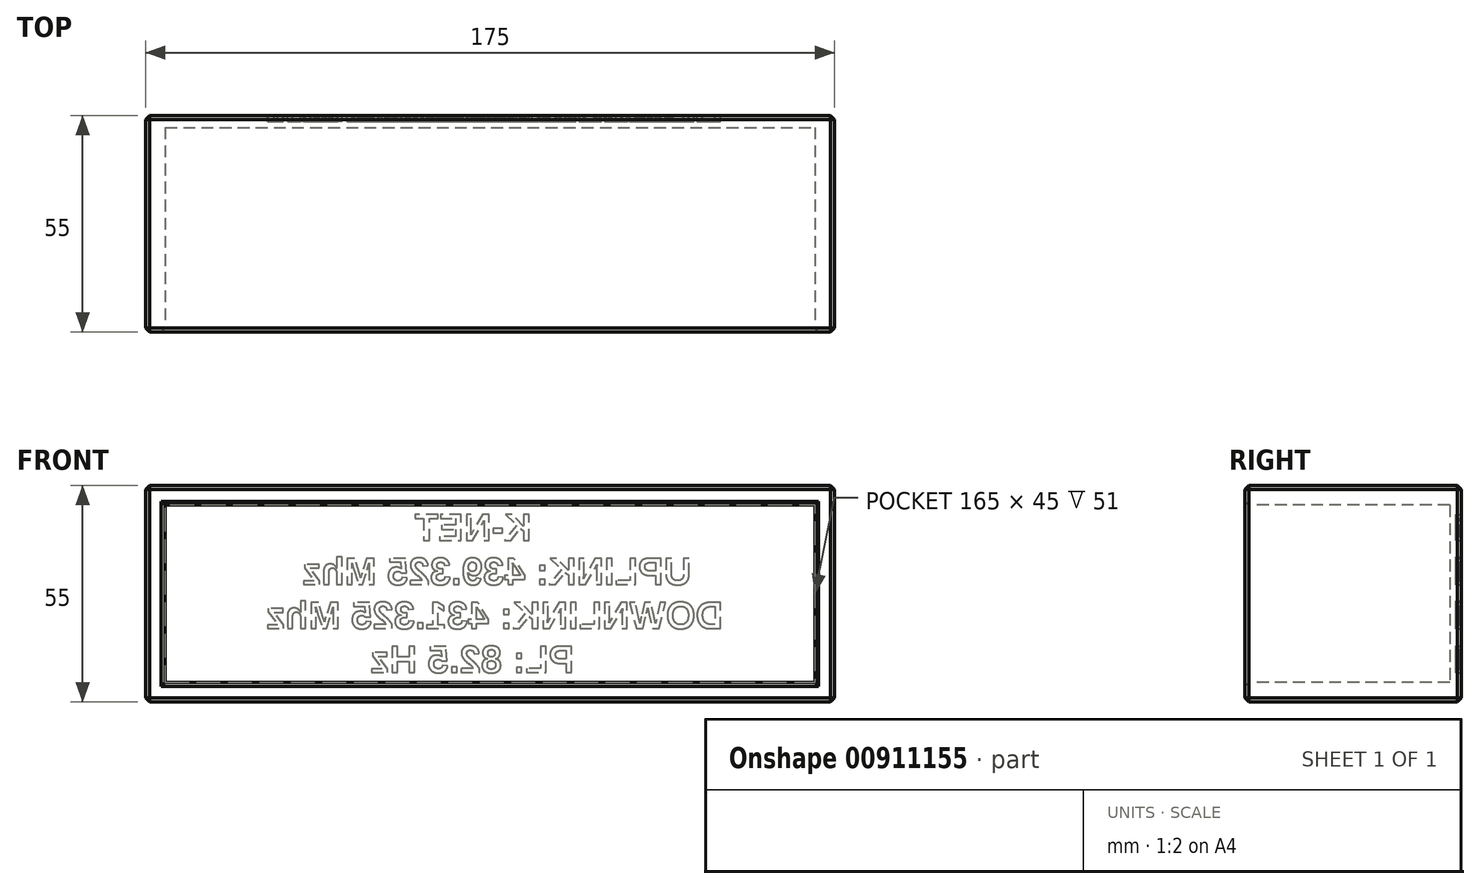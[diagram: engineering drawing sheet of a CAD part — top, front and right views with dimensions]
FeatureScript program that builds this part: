
annotation { "Feature Type Name" : "Feature", "Feature Type Description" : "" }
export const myFeature = defineFeature(function(context is Context, id is Id, definition is map)
    precondition{}
    {
        {
            var Q0;
            Q0=qCreatedBy(makeId("Front.planeOp"),FACE);
            var sketch = newSketch(context, id + "F0", { "sketchPlane" : qUnion([Q0])});
            skLineSegment(sketch, "E0.bottom", {"start": v(-83, 23) * mm, "end": v(92, 23) * mm});
            skLineSegment(sketch, "E0.top", {"start": v(-83, -32) * mm, "end": v(92, -32) * mm});
            skLineSegment(sketch, "E0.left", {"start": v(-83, 23) * mm, "end": v(-83, -32) * mm});
            skLineSegment(sketch, "E0.right", {"start": v(92, 23) * mm, "end": v(92, -32) * mm});
            skSolve(sketch);
        }
        {
            var Q0;
            Q0 = qSketchRegion(id + "F0", true);
            extrude(context, id + "F1", {"entities" : qUnion([Q0]), "depth" : 55 * mm, "offsetDistance" : 25 * mm});
        }
        {
            var Q0;
            Q0=makeQuery(id+"F1.opExtrude","CAP_FACE",FACE,{"disambiguationData":[OSD([sQuery(id+"F0.wireOp",EDGE,"E0.bottom"),sQuery(id+"F0.wireOp",EDGE,"E0.top"),sQuery(id+"F0.wireOp",EDGE,"E0.left"),sQuery(id+"F0.wireOp",EDGE,"E0.right")])],"isStart":false});
            var sketch = newSketch(context, id + "F2", { "sketchPlane" : qUnion([Q0])});
            skLineSegment(sketch, "E1.bottom", {"start": v(-78, 18) * mm, "end": v(87, 18) * mm});
            skLineSegment(sketch, "E1.top", {"start": v(-78, -27) * mm, "end": v(87, -27) * mm});
            skLineSegment(sketch, "E1.left", {"start": v(-78, 18) * mm, "end": v(-78, -27) * mm});
            skLineSegment(sketch, "E1.right", {"start": v(87, 18) * mm, "end": v(87, -27) * mm});
            skSolve(sketch);
        }
        {
            var Q0;
            Q0 = qSketchRegion(id + "F2", true);
            extrude(context, id + "F3", {"entities" : qUnion([Q0]), "operationType" : NewBodyOperationType.REMOVE, "oppositeDirection" : true, "depth" : 52 * mm, "offsetDistance" : 25 * mm});
        }
        {
            var Q0;
            Q0=makeQuery(id+"F1.opExtrude","CAP_FACE",FACE,{"disambiguationData":[OSD([sQuery(id+"F0.wireOp",EDGE,"E0.bottom"),sQuery(id+"F0.wireOp",EDGE,"E0.top"),sQuery(id+"F0.wireOp",EDGE,"E0.left"),sQuery(id+"F0.wireOp",EDGE,"E0.right")])],"isStart":false});
            var sketch = newSketch(context, id + "F4", { "sketchPlane" : qUnion([Q0])});
            skLineSegment(sketch, "E2.bottom", {"start": v(-78, 18) * mm, "end": v(87, 18) * mm});
            skLineSegment(sketch, "E2.top", {"start": v(-78, -27) * mm, "end": v(87, -27) * mm});
            skLineSegment(sketch, "E2.left", {"start": v(-78, 18) * mm, "end": v(-78, -27) * mm});
            skLineSegment(sketch, "E2.right", {"start": v(87, 18) * mm, "end": v(87, -27) * mm});
            skSolve(sketch);
        }
        {
            var Q0;
            Q0 = qSketchRegion(id + "F4", true);
            extrude(context, id + "F5", {"entities" : qUnion([Q0]), "operationType" : NewBodyOperationType.REMOVE, "oppositeDirection" : true, "depth" : 20 * mm, "offsetDistance" : 25 * mm});
        }
        {
            var Q0;
            Q0=makeQuery(id+"F1.opExtrude","SWEPT_EDGE",EDGE,{"disambiguationData":[OSD([sQuery(id+"F0.wireOp",EDGE,"E0.bottom"),sQuery(id+"F0.wireOp",EDGE,"E0.right")])]});
            var Q1;
            Q1=makeQuery(id+"F1.opExtrude","CAP_FACE",FACE,{"disambiguationData":[OSD([sQuery(id+"F0.wireOp",EDGE,"E0.bottom"),sQuery(id+"F0.wireOp",EDGE,"E0.top"),sQuery(id+"F0.wireOp",EDGE,"E0.left"),sQuery(id+"F0.wireOp",EDGE,"E0.right")])],"isStart":false});
            var Q2;
            Q2=makeQuery(id+"F1.opExtrude","CAP_EDGE",EDGE,{"disambiguationData":[OSD([sQuery(id+"F0.wireOp",EDGE,"E0.right")])],"isStart":true});
            var Q3;
            Q3=makeQuery(id+"F1.opExtrude","CAP_EDGE",EDGE,{"disambiguationData":[OSD([sQuery(id+"F0.wireOp",EDGE,"E0.bottom")])],"isStart":true});
            var Q4;
            Q4=makeQuery(id+"F1.opExtrude","CAP_EDGE",EDGE,{"disambiguationData":[OSD([sQuery(id+"F0.wireOp",EDGE,"E0.left")])],"isStart":true});
            var Q5;
            Q5=makeQuery(id+"F1.opExtrude","CAP_EDGE",EDGE,{"disambiguationData":[OSD([sQuery(id+"F0.wireOp",EDGE,"E0.top")])],"isStart":true});
            var Q6;
            Q6=makeQuery(id+"F1.opExtrude","SWEPT_EDGE",EDGE,{"disambiguationData":[OSD([sQuery(id+"F0.wireOp",EDGE,"E0.top"),sQuery(id+"F0.wireOp",EDGE,"E0.left")])]});
            var Q7;
            Q7=makeQuery(id+"F1.opExtrude","SWEPT_FACE",FACE,{"disambiguationData":[OSD([sQuery(id+"F0.wireOp",EDGE,"E0.right")])]});
            var Q8;
            Q8=makeQuery(id+"F1.opExtrude","SWEPT_EDGE",EDGE,{"disambiguationData":[OSD([sQuery(id+"F0.wireOp",EDGE,"E0.bottom"),sQuery(id+"F0.wireOp",EDGE,"E0.left")])]});
            chamfer(context, id + "F6", {"entities" : qUnion([Q0, Q1, Q2, Q3, Q4, Q5, Q6, Q7, Q8]), "width" : 1 * mm, "tangentPropagation" : true});
        }
        {
            var Q0;
            Q0=makeQuery(id+"F1.opExtrude","CAP_FACE",FACE,{"disambiguationData":[OSD([sQuery(id+"F0.wireOp",EDGE,"E0.bottom"),sQuery(id+"F0.wireOp",EDGE,"E0.top"),sQuery(id+"F0.wireOp",EDGE,"E0.left"),sQuery(id+"F0.wireOp",EDGE,"E0.right")])],"isStart":true});
            var sketch = newSketch(context, id + "F7", { "sketchPlane" : qUnion([Q0])});
            skText(sketch, "E3", { "text": "                  K-NET\n   UPLINK: 439.325 Mhz\nDOWNLINK: 431.325 Mhz\n              PL: 82.5 Hz", "fontName": "Arimo-Bold.ttf"});
            const initialGuessF7  = {"E3": [-0.06373, 0.009, 1, 0, 0.007]};
            skSetInitialGuess(sketch, initialGuessF7);
            skSolve(sketch);
        }
        {
            var Q0;
            Q0 = qSketchRegion(id + "F7", true);
            extrude(context, id + "F8", {"entities" : qUnion([Q0]), "operationType" : NewBodyOperationType.REMOVE, "oppositeDirection" : true, "depth" : 1.5 * mm, "offsetDistance" : 25 * mm});
        }
    });
